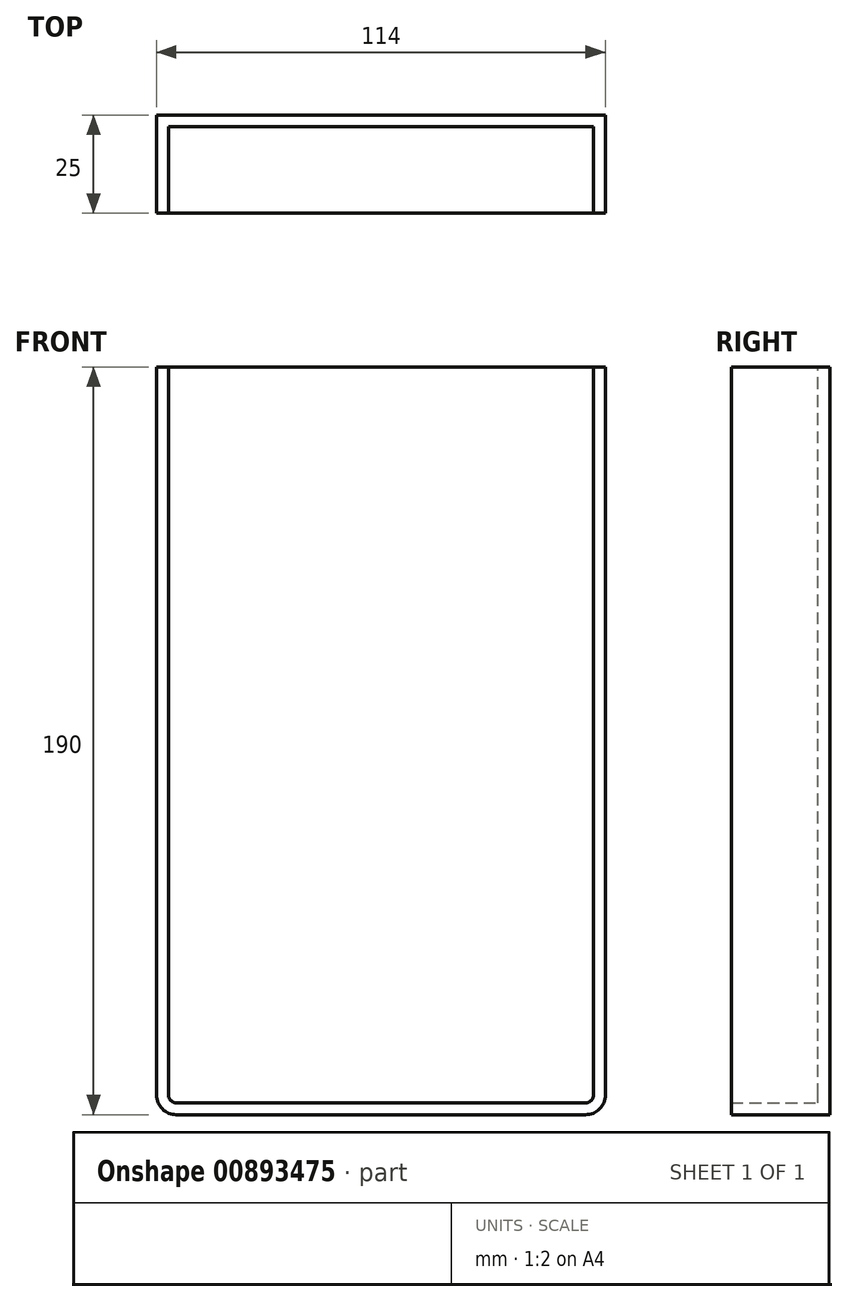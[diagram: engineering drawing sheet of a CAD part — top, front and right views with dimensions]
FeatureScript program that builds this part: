
annotation { "Feature Type Name" : "Feature", "Feature Type Description" : "" }
export const myFeature = defineFeature(function(context is Context, id is Id, definition is map)
    precondition{}
    {
        {
            var Q0;
            Q0=qCreatedBy(makeId("Front.planeOp"),FACE);
            var sketch = newSketch(context, id + "F0", { "sketchPlane" : qUnion([Q0])});
            skLineSegment(sketch, "E0.bottom", {"start": v(-57, -95) * mm, "end": v(57, -95) * mm});
            skLineSegment(sketch, "E0.top", {"start": v(-57, 95) * mm, "end": v(57, 95) * mm});
            skLineSegment(sketch, "E0.left", {"start": v(-57, -95) * mm, "end": v(-57, 95) * mm});
            skLineSegment(sketch, "E0.right", {"start": v(57, -95) * mm, "end": v(57, 95) * mm});
            skPoint(sketch, "E0.middle", {"position": v(0, 0) * mm});
            skSolve(sketch);
        }
        {
            var Q0;
            Q0 = qSketchRegion(id + "F0", true);
            extrude(context, id + "F1", {"entities" : qUnion([Q0]), "depth" : 25 * mm, "offsetDistance" : 25 * mm});
        }
        {
            var Q0;
            Q0=makeQuery(id+"F1.opExtrude","SWEPT_EDGE",EDGE,{"disambiguationData":[OSD([sQuery(id+"F0.wireOp",EDGE,"E0.bottom"),sQuery(id+"F0.wireOp",EDGE,"E0.right")])]});
            var Q1;
            Q1=makeQuery(id+"F1.opExtrude","SWEPT_EDGE",EDGE,{"disambiguationData":[OSD([sQuery(id+"F0.wireOp",EDGE,"E0.bottom"),sQuery(id+"F0.wireOp",EDGE,"E0.left")])]});
            fillet(context, id + "F2", {"entities" : qUnion([Q0, Q1]), "radius" : 5 * mm, "allowEdgeOverflow" : false});
        }
        {
            var Q0;
            Q0=makeQuery(id+"F1.opExtrude","CAP_FACE",FACE,{"disambiguationData":[OSD([sQuery(id+"F0.wireOp",EDGE,"E0.bottom"),sQuery(id+"F0.wireOp",EDGE,"E0.top"),sQuery(id+"F0.wireOp",EDGE,"E0.left"),sQuery(id+"F0.wireOp",EDGE,"E0.right")])],"isStart":false});
            var Q1;
            Q1=makeQuery(id+"F1.opExtrude","SWEPT_FACE",FACE,{"disambiguationData":[OSD([sQuery(id+"F0.wireOp",EDGE,"E0.top")])]});
            shell(context, id + "F3", {"entities" : qUnion([Q0, Q1]), "thickness" : 3 * mm});
        }
    });
